# Revit family: MARIONA_21W_3000K_1300LM_NOIR
name_source: partatom
category: Lighting Fixtures
units: mm (PartAtom-declared; Revit-internal decimal feet)

## family parameters
Always vertical = Yes
Cut with Voids When Loaded = No
Host = Wall
Light Source = Yes
OmniClass Number = 23.80.70.00
OmniClass Title = Lighting
Part Type = Normal
Room Calculation Point = No
Round Connector Dimension = Use Diameter
Shared = No

## types (1)
- Type 1
    Alimentation Driver = AC 220-240V
    Alimentation luminaire = 300mA
    Color Filter = 16777215
    Default Elevation = 0 mm  [stored 0 ft]
    Diffuseur = Polycarbonate
    Dimensions = 320 x 133 x 134 mm
    Dimming Lamp Color Temperature Shift = <None>
    Driver = Driver Kegu 500mA
    Emit from Line Length = 610 mm
    Fintion = Noir
    Light Source Symbol Size = 610 mm
    Matériau = ABS
    Puissance nominale = 21W
    Type = Applique murale
    Type de lampe = 2835 SMD LED

note: [stored X ft] marks values corroborated as IEEE doubles in the binary element streams (Revit-internal decimal feet)

## geometry (parser evidence)
native form markers: Sweep x3
no freeform markers — native parametric forms only
